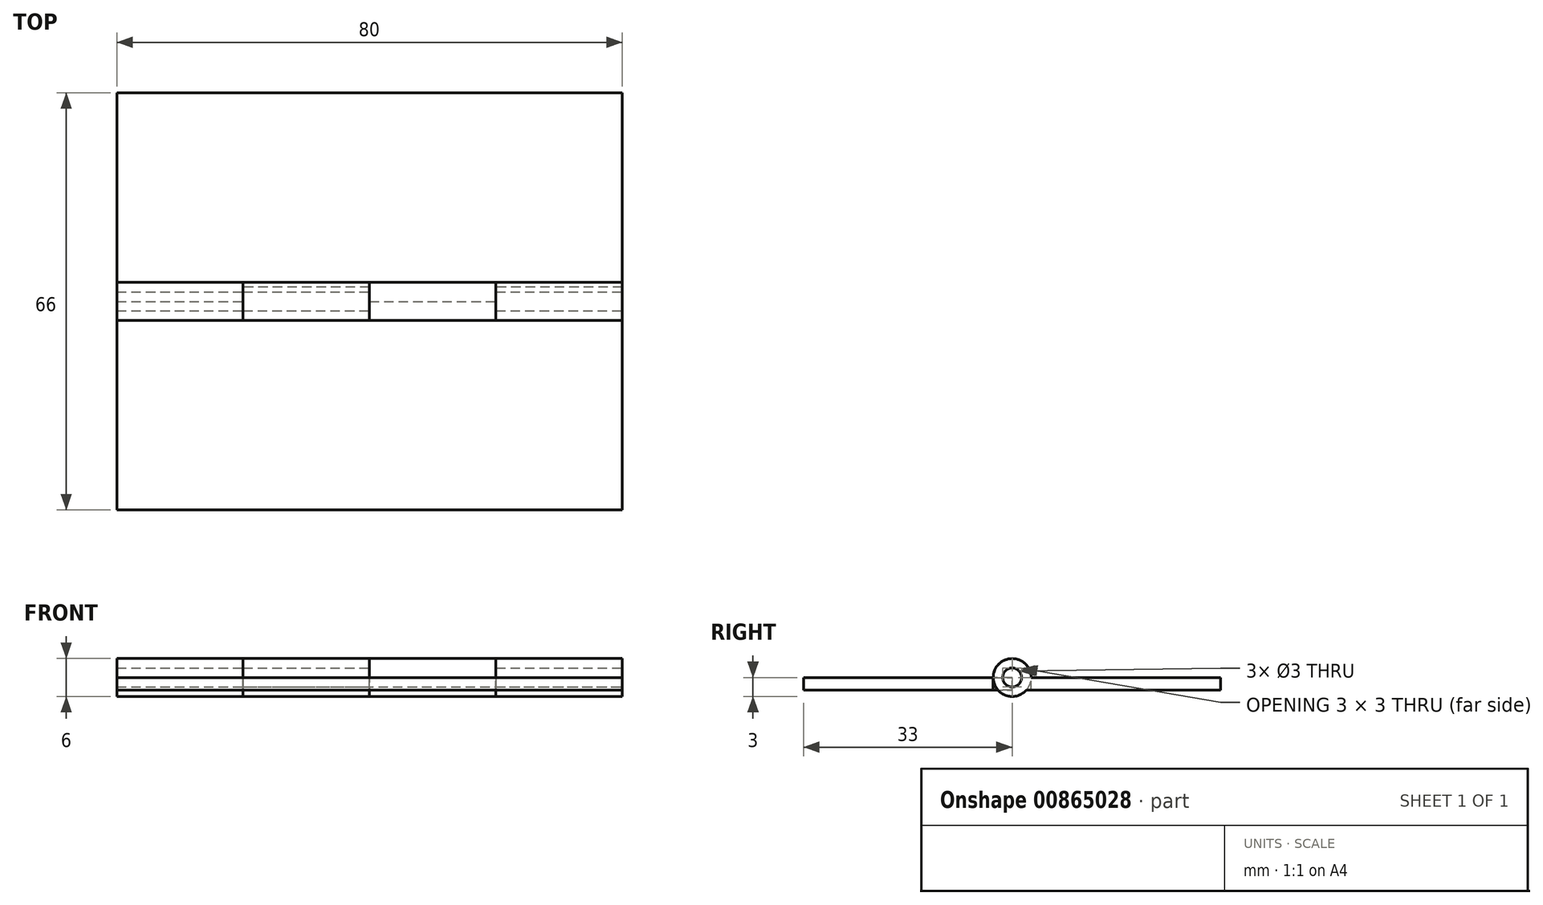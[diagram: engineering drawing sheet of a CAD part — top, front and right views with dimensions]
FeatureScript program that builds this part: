
annotation { "Feature Type Name" : "Feature", "Feature Type Description" : "" }
export const myFeature = defineFeature(function(context is Context, id is Id, definition is map)
    precondition{}
    {
        {
            var Q0;
            Q0=qCreatedBy(makeId("Top.planeOp"),FACE);
            var sketch = newSketch(context, id + "F0", { "sketchPlane" : qUnion([Q0])});
            skLineSegment(sketch, "E0.bottom", {"start": v(40, -18) * mm, "end": v(-40, -18) * mm});
            skLineSegment(sketch, "E0.left", {"start": v(40, -18) * mm, "end": v(40, 12) * mm});
            skLineSegment(sketch, "E0.right", {"start": v(-40, -18) * mm, "end": v(-40, 18) * mm});
            skPoint(sketch, "E0.middle", {"position": v(0, 0) * mm});
            skLineSegment(sketch, "E1", {"start": v(-40, 18) * mm, "end": v(-20, 18) * mm});
            skLineSegment(sketch, "E2", {"start": v(-20, 18) * mm, "end": v(-20, 12) * mm});
            skLineSegment(sketch, "E3", {"start": v(-20, 12) * mm, "end": v(0, 12) * mm});
            skLineSegment(sketch, "E4", {"start": v(0, 12) * mm, "end": v(0, 18) * mm});
            skLineSegment(sketch, "E5", {"start": v(0, 18) * mm, "end": v(20, 18) * mm});
            skLineSegment(sketch, "E6", {"start": v(20, 18) * mm, "end": v(20, 12) * mm});
            skLineSegment(sketch, "E7", {"start": v(20, 12) * mm, "end": v(40, 12) * mm});
            skLineSegment(sketch, "E8", {"start": v(-40, 18) * mm, "end": v(-40, 48) * mm});
            skLineSegment(sketch, "E9", {"start": v(-40, 48) * mm, "end": v(40, 48) * mm});
            skLineSegment(sketch, "E10", {"start": v(40, 48) * mm, "end": v(40, 12) * mm});
            skLineSegment(sketch, "E11", {"start": v(-40, 15) * mm, "end": v(40, 15) * mm});
            skPoint(sketch, "E11.startSnap0", {"position": v(-20, 15) * mm});
            skLineSegment(sketch, "E12", {"start": v(-20, 12) * mm, "end": v(-40, 12) * mm, "construction": true});
            skLineSegment(sketch, "E13", {"start": v(-20, 18) * mm, "end": v(0, 18) * mm, "construction": true});
            skLineSegment(sketch, "E14", {"start": v(0, 12) * mm, "end": v(20, 12) * mm, "construction": true});
            skLineSegment(sketch, "E15", {"start": v(20, 18) * mm, "end": v(40, 18) * mm, "construction": true});
            skSolve(sketch);
        }
        {
            var Q0;
            Q0=makeQuery(id+"F0.imprint","IMPRINT",FACE,{"disambiguationData":[TD([[makeQuery(id+"F0.imprint","IMPRINT",EDGE,{"derivedFrom":sQuery(id+"F0.wireOp",EDGE,"E1")}),1.0]])]});
            extrude(context, id + "F1", {"entities" : qUnion([Q0]), "oppositeDirection" : true, "depth" : 2 * mm, "offsetDistance" : 25 * mm});
        }
        {
            var Q0;
            Q0=makeQuery(id+"F0.imprint","IMPRINT",FACE,{"disambiguationData":[TD([[makeQuery(id+"F0.imprint","IMPRINT",EDGE,{"derivedFrom":sQuery(id+"F0.wireOp",EDGE,"E0.bottom")}),-1.0]])]});
            extrude(context, id + "F2", {"entities" : qUnion([Q0]), "oppositeDirection" : true, "depth" : 2 * mm, "offsetDistance" : 25 * mm});
        }
        {
            var Q0;
            {var subQ0=sQuery(id+"F0.wireOp",EDGE,"E1");Q0=makeQuery(id+"F0.imprint","IMPRINT",FACE,{"disambiguationData":[TD([[makeQuery(id+"F0.imprint","IMPRINT",EDGE,{"derivedFrom":subQ0}),-1.0]])]});}
            var Q1;
            {var subQ0=sQuery(id+"F0.wireOp",EDGE,"E5");Q1=makeQuery(id+"F0.imprint","IMPRINT",FACE,{"disambiguationData":[TD([[makeQuery(id+"F0.imprint","IMPRINT",EDGE,{"derivedFrom":subQ0}),-1.0]])]});}
            var Q2;
            Q2=sQuery(id+"F0.wireOp",EDGE,"E11");
            revolve(context, id + "F3", {"surfaceOperationType" : NewSurfaceOperationType.NEW, "entities" : qUnion([Q0, Q1]), "axis" : qUnion([Q2]), "revolveType" : RevolveType.FULL});
        }
        {
            var Q0;
            {var subQ0=sQuery(id+"F0.wireOp",EDGE,"E3");Q0=makeQuery(id+"F0.imprint","IMPRINT",FACE,{"disambiguationData":[TD([[makeQuery(id+"F0.imprint","IMPRINT",EDGE,{"derivedFrom":subQ0}),1.0]])]});}
            var Q1;
            {var subQ0=sQuery(id+"F0.wireOp",EDGE,"E7");Q1=makeQuery(id+"F0.imprint","IMPRINT",FACE,{"disambiguationData":[TD([[makeQuery(id+"F0.imprint","IMPRINT",EDGE,{"derivedFrom":subQ0}),1.0]])]});}
            var Q2;
            Q2=sQuery(id+"F0.wireOp",EDGE,"E11");
            revolve(context, id + "F4", {"surfaceOperationType" : NewSurfaceOperationType.NEW, "entities" : qUnion([Q0, Q1]), "axis" : qUnion([Q2]), "revolveType" : RevolveType.FULL});
        }
        {
            var Q0;
            Q0=makeQuery(id+"F1.opExtrude","SWEPT_BODY",BODY,{"disambiguationData":[OSD([sQuery(id+"F0.wireOp",EDGE,"E1"),sQuery(id+"F0.wireOp",EDGE,"E2"),sQuery(id+"F0.wireOp",EDGE,"E4"),sQuery(id+"F0.wireOp",EDGE,"E5"),sQuery(id+"F0.wireOp",EDGE,"E6"),sQuery(id+"F0.wireOp",EDGE,"E8"),sQuery(id+"F0.wireOp",EDGE,"E9"),sQuery(id+"F0.wireOp",EDGE,"E10"),sQuery(id+"F0.wireOp",EDGE,"E11")])]});
            var Q1;
            Q1=makeQuery(id+"F4.opRevolve","SWEPT_BODY",BODY,{"disambiguationData":[OSD([sQuery(id+"F0.wireOp",EDGE,"E2"),sQuery(id+"F0.wireOp",EDGE,"E3"),sQuery(id+"F0.wireOp",EDGE,"E4"),sQuery(id+"F0.wireOp",EDGE,"E11")])]});
            var Q2;
            Q2=makeQuery(id+"F4.opRevolve","SWEPT_BODY",BODY,{"disambiguationData":[OSD([sQuery(id+"F0.wireOp",EDGE,"E6"),sQuery(id+"F0.wireOp",EDGE,"E7"),sQuery(id+"F0.wireOp",EDGE,"E10"),sQuery(id+"F0.wireOp",EDGE,"E11")])]});
            booleanBodies(context, id + "F5", {"operationType" : BooleanOperationType.UNION, "tools" : qUnion([Q0, Q1, Q2])});
        }
        {
            var Q0;
            {var subQ0=sQuery(id+"F0.wireOp",EDGE,"E10");Q0=makeQuery(id+"F5.opBoolean","MERGE",FACE,{"derivedFrom":[makeQuery(id+"F1.opExtrude","SWEPT_FACE",FACE,{"disambiguationData":[OSD([subQ0])]}),makeQuery(id+"F4.opRevolve","SWEPT_FACE",FACE,{"disambiguationData":[OSD([subQ0])]})]});}
            var sketch = newSketch(context, id + "F6", { "sketchPlane" : qUnion([Q0])});
            skCircle(sketch, "E16", {"center": v(15, 0) * mm, "radius": 1.5 * mm});
            skSolve(sketch);
        }
        {
            var Q0;
            Q0=sQuery(id+"F6.wireOp",VERTEX,"E16.center");
            var Q1;
            Q1=makeQuery(id+"F1.opExtrude","SWEPT_BODY",BODY,{"disambiguationData":[OSD([sQuery(id+"F0.wireOp",EDGE,"E1"),sQuery(id+"F0.wireOp",EDGE,"E2"),sQuery(id+"F0.wireOp",EDGE,"E4"),sQuery(id+"F0.wireOp",EDGE,"E5"),sQuery(id+"F0.wireOp",EDGE,"E6"),sQuery(id+"F0.wireOp",EDGE,"E8"),sQuery(id+"F0.wireOp",EDGE,"E9"),sQuery(id+"F0.wireOp",EDGE,"E10"),sQuery(id+"F0.wireOp",EDGE,"E11")])]});
            var Q2;
            Q2=makeQuery(id+"F3.opRevolve","SWEPT_BODY",BODY,{"disambiguationData":[OSD([sQuery(id+"F0.wireOp",EDGE,"E0.right"),sQuery(id+"F0.wireOp",EDGE,"E1"),sQuery(id+"F0.wireOp",EDGE,"E2"),sQuery(id+"F0.wireOp",EDGE,"E11")])]});
            hole(context, id + "F7", {"style" : HoleStyle.SIMPLE, "endStyle" : HoleEndStyle.THROUGH, "holeDiameter" : 3 * mm, "majorDiameter" : 5 * mm, "isTappedThrough" : true, "tappedDepth" : 12 * mm, "tapClearance" : 3, "locations" : qUnion([Q0]), "scope" : qUnion([Q1, Q2])});
        }
        {
            var Q0;
            Q0=makeQuery(id+"F6.imprint","IMPRINT",FACE,{"disambiguationData":[TD([[makeQuery(id+"F6.imprint","IMPRINT",EDGE,{"derivedFrom":sQuery(id+"F6.wireOp",EDGE,"E16")}),1.0]])]});
            extrude(context, id + "F8", {"entities" : qUnion([Q0]), "oppositeDirection" : true, "depth" : 80 * mm, "offsetDistance" : 25 * mm});
        }
    });
